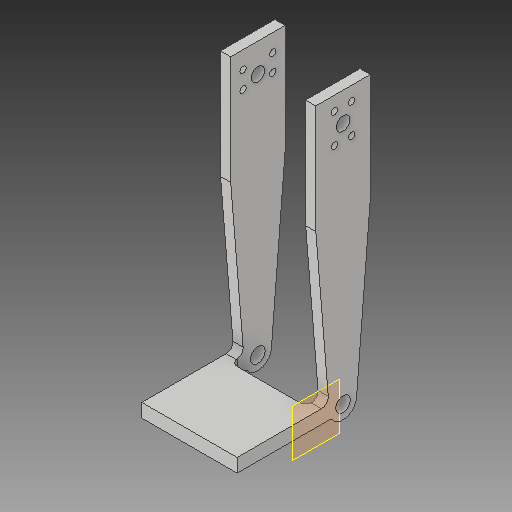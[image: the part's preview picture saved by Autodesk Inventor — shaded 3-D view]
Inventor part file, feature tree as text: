
AUTODESK INVENTOR PART (.ipt)
format: ipt  version: 2017 (Build 210142000, 142)  size: 245,248 bytes
history: native  units: in
note: dims shown in document units (in); Inventor stores cm internally (conversion verified against a paired STEP export)
features: sketch x9, projected_geometry x9, hole x5, extrude x4, plane x2, fillet x2
ambient origin geometry x8: Origin, YZ Plane, XZ Plane, XY Plane, X Axis, Y Axis, Z Axis, Center Point
bodies: Solid1 (feature_tree)
feature tree (31):
  sketch  "Sketch1"  dims[d0=5.0in d1=1.0in]
  plane  "Work Plane1"
  extrude  "Extrusion2"  Depth=1.0in
  plane  "Work Plane2"
  extrude  "Extrusion3"  Depth=0.5in
  hole  "Hole2"  [1 undecoded]
  extrude  "Extrusion4"  Depth=0.5in
  extrude  "Extrusion5"  Depth=1.753in
  fillet  "Fillet1"  Radius=2.0in
  fillet  "Fillet2"  Radius=1.753in
  hole  "Hole3"  [1 undecoded]
  hole  "Hole4"  [1 undecoded]
  hole  "Hole5"  [1 undecoded]
  hole  "Hole6"  [1 undecoded]
  sketch  "Sketch2"  dims[d5=1.0in d6=0.5in]
  projected_geometry  "Projected Loop1"
  sketch  "Sketch4"  dims[d7=0.5in d8=0.0in]
  projected_geometry  "Projected Loop3"
  sketch  "Sketch5"  dims[d9=1.753in d10=0.0in d18=0.5in]
  projected_geometry  "Projected Loop4"
  sketch  "Sketch8"  dims[d19=0.25in d20=2.0in d21=2.0in d22=1.753in d23=0.0in]
  projected_geometry  "Projected Loop9"
  projected_geometry  "Projected Loop10"
  sketch  "Sketch9"  dims[d24=0.27in d25=0.75in d26=0.375in d27=0.25in d28=0.5635in d29=1.0in d30=0.8108in d31=1.75in]
  projected_geometry  "Projected Loop11"
  sketch  "Sketch10"  dims[d32=0.25in d35=5.0in]
  projected_geometry  "Projected Loop12"
  sketch  "Sketch11"  dims[d36=4.875in d37=1.753in d38=0.0in]
  projected_geometry  "Projected Loop13"
  sketch  "Sketch12"  dims[d41=1.753in d42=5.375in d43=1.378in d44=0.1875in d45=5.875in d46=1.0in d47=0.0in d48=0.125in d49=0.125in d50=0.6299in d51=1.0in d52=0.5in d53=0.315in d54=0.1575in d55=0.117in d56=0.75in d57=0.375in d58=0.25in d59=0.5635in d60=1.0in d61=0.8108in d62=0.6299in d63=1.0in d64=0.5in d65=0.315in d66=0.1575in d67=0.117in d68=0.75in d69=0.375in d70=0.25in d71=0.5635in d72=1.0in d73=0.8108in d74=0.32in d75=1.753in d77=0.5in d78=0.75in d79=0.375in d80=0.25in d81=0.5635in d82=0.125in d83=0.0in d84=1.0in d85=0.5in d86=0.5455in d87=0.2728in d88=0.25in d89=0.75in d90=0.375in d91=0.25in d92=0.5635in d93=1.0in d94=0.8108in d95=0.27in d96=0.1975in d97=0.375in]
  projected_geometry  "Projected Loop14"
note: 5 required parameter values undecoded (feature->parameter linkage not recoverable at this tier; creation-order binding heuristic only, values carry confidence <= 0.55)
